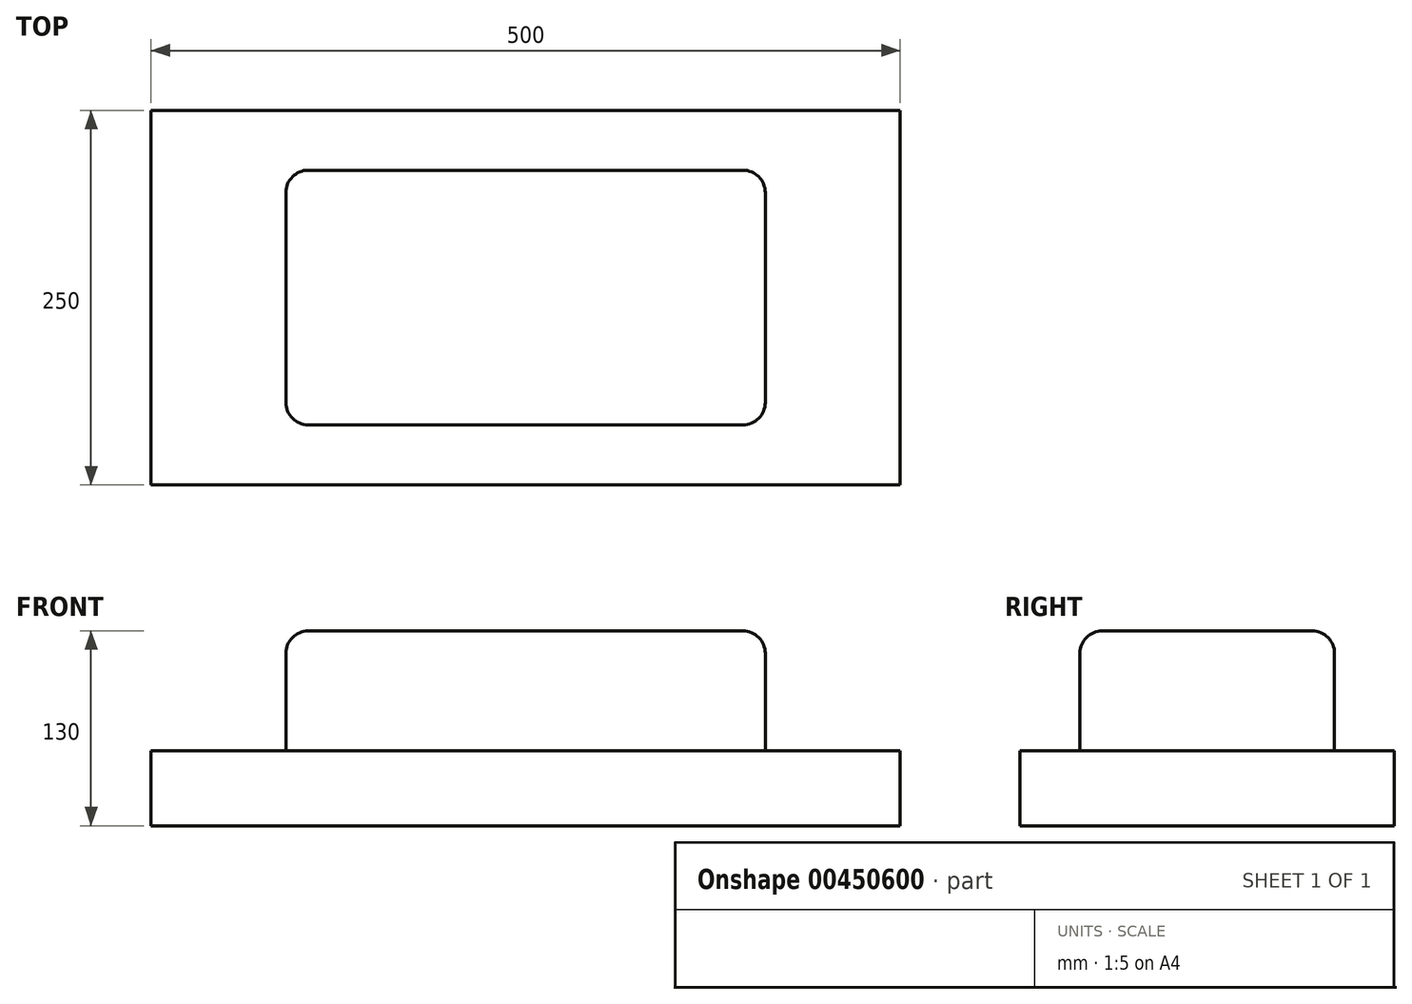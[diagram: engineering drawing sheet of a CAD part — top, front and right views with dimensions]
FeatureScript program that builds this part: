
annotation { "Feature Type Name" : "Feature", "Feature Type Description" : "" }
export const myFeature = defineFeature(function(context is Context, id is Id, definition is map)
    precondition{}
    {
        {
            var Q0;
            Q0=qCreatedBy(makeId("Top.planeOp"),FACE);
            var sketch = newSketch(context, id + "F0", { "sketchPlane" : qUnion([Q0])});
            skLineSegment(sketch, "E0.bottom", {"start": v(-250, -125) * mm, "end": v(250, -125) * mm});
            skLineSegment(sketch, "E0.top", {"start": v(-250, 125) * mm, "end": v(250, 125) * mm});
            skLineSegment(sketch, "E0.left", {"start": v(-250, -125) * mm, "end": v(-250, 125) * mm});
            skLineSegment(sketch, "E0.right", {"start": v(250, -125) * mm, "end": v(250, 125) * mm});
            skPoint(sketch, "E0.middle", {"position": v(0, 0) * mm});
            skSolve(sketch);
        }
        {
            var Q0;
            Q0=makeQuery(id+"F0.imprint","IMPRINT",FACE,{"disambiguationData":[TD([[makeQuery(id+"F0.imprint","IMPRINT",EDGE,{"derivedFrom":sQuery(id+"F0.wireOp",EDGE,"E0.bottom")}),1.0]])]});
            extrude(context, id + "F1", {"entities" : qUnion([Q0]), "endBound" : BoundingType.SYMMETRIC, "depth" : 50 * mm});
        }
        {
            var Q0;
            Q0=makeQuery(id+"F1.opExtrude","CAP_FACE",FACE,{"disambiguationData":[OSD([sQuery(id+"F0.wireOp",EDGE,"E0.bottom"),sQuery(id+"F0.wireOp",EDGE,"E0.top"),sQuery(id+"F0.wireOp",EDGE,"E0.left"),sQuery(id+"F0.wireOp",EDGE,"E0.right")])],"isStart":false});
            var sketch = newSketch(context, id + "F2", { "sketchPlane" : qUnion([Q0])});
            skLineSegment(sketch, "E1.bottom", {"start": v(-160, -85) * mm, "end": v(160, -85) * mm});
            skLineSegment(sketch, "E1.top", {"start": v(-160, 85) * mm, "end": v(160, 85) * mm});
            skLineSegment(sketch, "E1.left", {"start": v(-160, -85) * mm, "end": v(-160, 85) * mm});
            skLineSegment(sketch, "E1.right", {"start": v(160, -85) * mm, "end": v(160, 85) * mm});
            skPoint(sketch, "E1.middle", {"position": v(0, 0) * mm});
            skSolve(sketch);
        }
        {
            var Q0;
            Q0=qSketchRegion(id+"F2",true);
            extrude(context, id + "F3", {"entities" : qUnion([Q0]), "operationType" : NewBodyOperationType.ADD, "depth" : 80 * mm});
        }
        {
            var Q0;
            Q0=makeQuery(id+"F3.opExtrude","CAP_EDGE",EDGE,{"disambiguationData":[OSD([sQuery(id+"F2.wireOp",EDGE,"E1.bottom")])],"isStart":false});
            var Q1;
            Q1=makeQuery(id+"F3.opExtrude","CAP_EDGE",EDGE,{"disambiguationData":[OSD([sQuery(id+"F2.wireOp",EDGE,"E1.left")])],"isStart":false});
            var Q2;
            Q2=makeQuery(id+"F3.opExtrude","CAP_EDGE",EDGE,{"disambiguationData":[OSD([sQuery(id+"F2.wireOp",EDGE,"E1.right")])],"isStart":false});
            var Q3;
            Q3=makeQuery(id+"F3.opExtrude","SWEPT_EDGE",EDGE,{"disambiguationData":[OSD([sQuery(id+"F2.wireOp",EDGE,"E1.bottom"),sQuery(id+"F2.wireOp",EDGE,"E1.left")])]});
            var Q4;
            Q4=makeQuery(id+"F3.opExtrude","SWEPT_EDGE",EDGE,{"disambiguationData":[OSD([sQuery(id+"F2.wireOp",EDGE,"E1.top"),sQuery(id+"F2.wireOp",EDGE,"E1.left")])]});
            var Q5;
            Q5=makeQuery(id+"F3.opExtrude","SWEPT_EDGE",EDGE,{"disambiguationData":[OSD([sQuery(id+"F2.wireOp",EDGE,"E1.bottom"),sQuery(id+"F2.wireOp",EDGE,"E1.right")])]});
            var Q6;
            Q6=makeQuery(id+"F3.opExtrude","CAP_EDGE",EDGE,{"disambiguationData":[OSD([sQuery(id+"F2.wireOp",EDGE,"E1.top")])],"isStart":false});
            var Q7;
            Q7=makeQuery(id+"F3.opExtrude","SWEPT_EDGE",EDGE,{"disambiguationData":[OSD([sQuery(id+"F2.wireOp",EDGE,"E1.top"),sQuery(id+"F2.wireOp",EDGE,"E1.right")])]});
            var Q8;
            Q8=makeQuery(id+"F3.opExtrude","CAP_EDGE",EDGE,{"disambiguationData":[OSD([sQuery(id+"F2.wireOp",EDGE,"E1.bottom")])],"isStart":true});
            fillet(context, id + "F4", {"entities" : qUnion([Q0, Q1, Q2, Q3, Q4, Q5, Q6, Q7, Q8]), "radius" : 15 * mm, "tangentPropagation" : true, "allowEdgeOverflow" : false});
        }
    });
